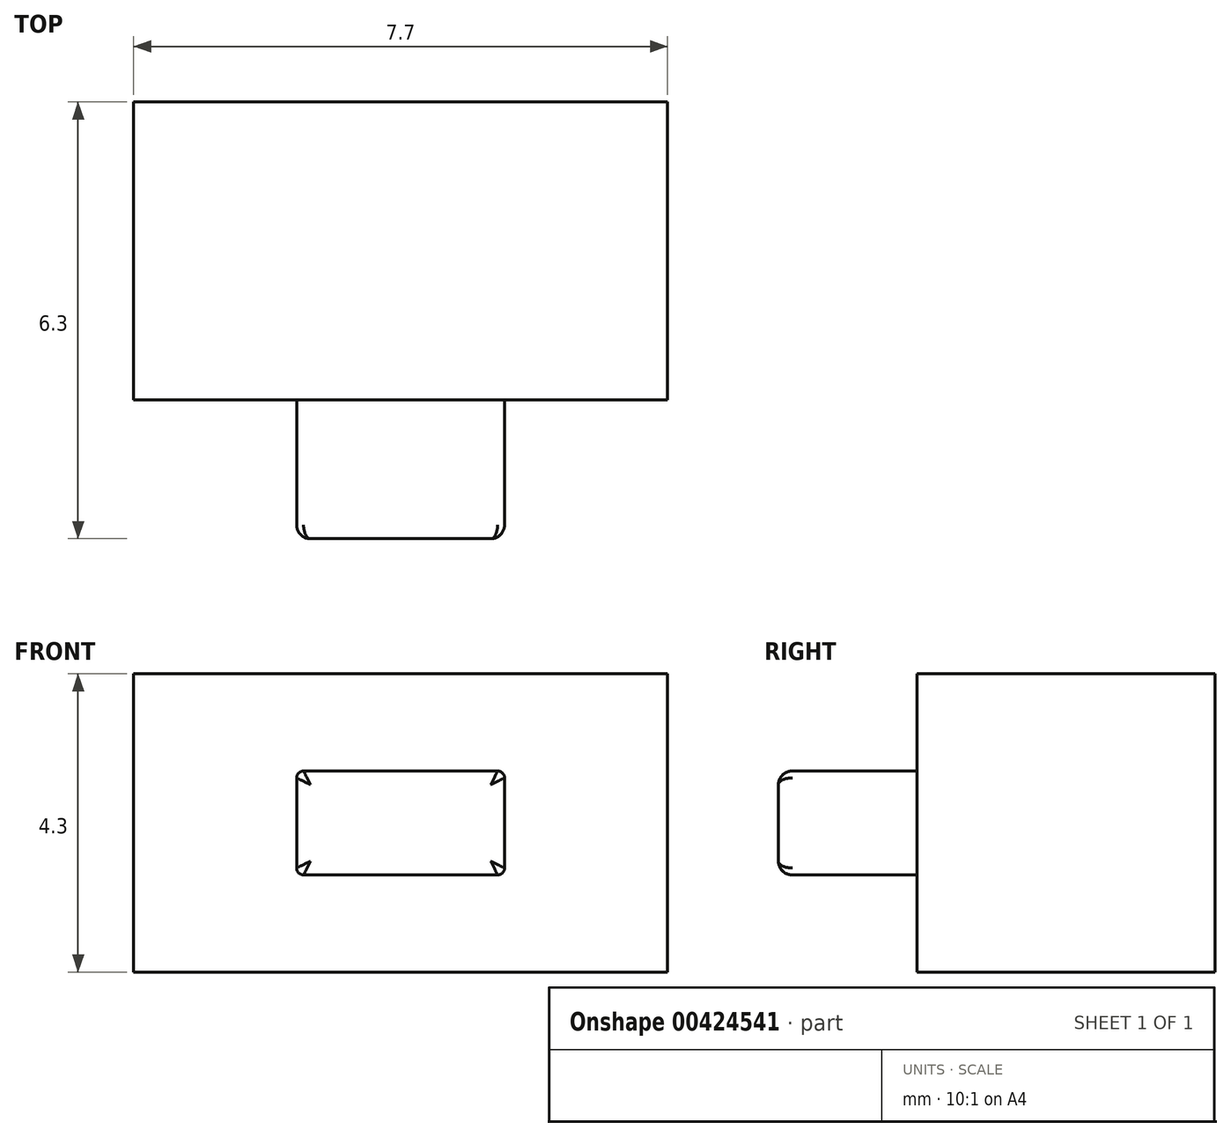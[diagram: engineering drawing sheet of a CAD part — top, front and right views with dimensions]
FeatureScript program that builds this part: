
annotation { "Feature Type Name" : "Feature", "Feature Type Description" : "" }
export const myFeature = defineFeature(function(context is Context, id is Id, definition is map)
    precondition{}
    {
        {
            var Q0;
            Q0=qCreatedBy(makeId("Front.planeOp"),FACE);
            var sketch = newSketch(context, id + "F0", { "sketchPlane" : qUnion([Q0])});
            skLineSegment(sketch, "E0.bottom", {"start": v(3.85, -2.15) * mm, "end": v(-3.85, -2.15) * mm});
            skLineSegment(sketch, "E0.top", {"start": v(3.85, 2.15) * mm, "end": v(-3.85, 2.15) * mm});
            skLineSegment(sketch, "E0.left", {"start": v(3.85, -2.15) * mm, "end": v(3.85, 2.15) * mm});
            skLineSegment(sketch, "E0.right", {"start": v(-3.85, -2.15) * mm, "end": v(-3.85, 2.15) * mm});
            skPoint(sketch, "E0.middle", {"position": v(0, 0) * mm});
            skLineSegment(sketch, "E1.bottom", {"start": v(1.5, -0.75) * mm, "end": v(-1.5, -0.75) * mm});
            skLineSegment(sketch, "E1.top", {"start": v(1.5, 0.75) * mm, "end": v(-1.5, 0.75) * mm});
            skLineSegment(sketch, "E1.left", {"start": v(1.5, -0.75) * mm, "end": v(1.5, 0.75) * mm});
            skLineSegment(sketch, "E1.right", {"start": v(-1.5, -0.75) * mm, "end": v(-1.5, 0.75) * mm});
            skSolve(sketch);
        }
        {
            var Q0;
            Q0=makeQuery(id+"F0.imprint","IMPRINT",FACE,{"disambiguationData":[TD([[makeQuery(id+"F0.imprint","IMPRINT",EDGE,{"derivedFrom":sQuery(id+"F0.wireOp",EDGE,"E0.bottom")}),-1.0]])]});
            var Q1;
            Q1=makeQuery(id+"F0.imprint","IMPRINT",FACE,{"disambiguationData":[TD([[makeQuery(id+"F0.imprint","IMPRINT",EDGE,{"derivedFrom":sQuery(id+"F0.wireOp",EDGE,"E1.bottom")}),-1.0]])]});
            extrude(context, id + "F1", {"entities" : qUnion([Q0, Q1]), "oppositeDirection" : true, "depth" : 4.3 * mm});
        }
        {
            var Q0;
            Q0=makeQuery(id+"F0.imprint","IMPRINT",FACE,{"disambiguationData":[TD([[makeQuery(id+"F0.imprint","IMPRINT",EDGE,{"derivedFrom":sQuery(id+"F0.wireOp",EDGE,"E1.bottom")}),-1.0]])]});
            extrude(context, id + "F2", {"entities" : qUnion([Q0]), "operationType" : NewBodyOperationType.ADD, "depth" : 2 * mm});
        }
        {
            var Q0;
            Q0=makeQuery(id+"F2.opExtrude","CAP_EDGE",EDGE,{"disambiguationData":[OSD([sQuery(id+"F0.wireOp",EDGE,"E1.top")])],"isStart":false});
            var Q1;
            Q1=makeQuery(id+"F2.opExtrude","CAP_EDGE",EDGE,{"disambiguationData":[OSD([sQuery(id+"F0.wireOp",EDGE,"E1.left")])],"isStart":false});
            var Q2;
            Q2=makeQuery(id+"F2.opExtrude","CAP_EDGE",EDGE,{"disambiguationData":[OSD([sQuery(id+"F0.wireOp",EDGE,"E1.bottom")])],"isStart":false});
            var Q3;
            Q3=makeQuery(id+"F2.opExtrude","CAP_EDGE",EDGE,{"disambiguationData":[OSD([sQuery(id+"F0.wireOp",EDGE,"E1.right")])],"isStart":false});
            fillet(context, id + "F3", {"entities" : qUnion([Q0, Q1, Q2, Q3]), "radius" : .2 * mm, "tangentPropagation" : true, "allowEdgeOverflow" : false});
        }
        {
            var Q0;
            Q0=makeQuery(id+"F3.opFillet","BLEND_EDGE",EDGE,{"blendedFrom":[makeQuery(id+"F2.opExtrude","CAP_EDGE",EDGE,{"disambiguationData":[OSD([sQuery(id+"F0.wireOp",EDGE,"E1.top")])],"isStart":false}),makeQuery(id+"F2.opExtrude","CAP_EDGE",EDGE,{"disambiguationData":[OSD([sQuery(id+"F0.wireOp",EDGE,"E1.left")])],"isStart":false})],"blendedInto":[]});
            var Q1;
            Q1=makeQuery(id+"F3.opFillet","BLEND_EDGE",EDGE,{"blendedFrom":[makeQuery(id+"F2.opExtrude","CAP_EDGE",EDGE,{"disambiguationData":[OSD([sQuery(id+"F0.wireOp",EDGE,"E1.bottom")])],"isStart":false}),makeQuery(id+"F2.opExtrude","CAP_EDGE",EDGE,{"disambiguationData":[OSD([sQuery(id+"F0.wireOp",EDGE,"E1.left")])],"isStart":false})],"blendedInto":[]});
            var Q2;
            Q2=makeQuery(id+"F3.opFillet","BLEND_EDGE",EDGE,{"blendedFrom":[makeQuery(id+"F2.opExtrude","CAP_EDGE",EDGE,{"disambiguationData":[OSD([sQuery(id+"F0.wireOp",EDGE,"E1.bottom")])],"isStart":false}),makeQuery(id+"F2.opExtrude","CAP_EDGE",EDGE,{"disambiguationData":[OSD([sQuery(id+"F0.wireOp",EDGE,"E1.right")])],"isStart":false})],"blendedInto":[]});
            var Q3;
            Q3=makeQuery(id+"F3.opFillet","BLEND_EDGE",EDGE,{"blendedFrom":[makeQuery(id+"F2.opExtrude","CAP_EDGE",EDGE,{"disambiguationData":[OSD([sQuery(id+"F0.wireOp",EDGE,"E1.top")])],"isStart":false}),makeQuery(id+"F2.opExtrude","CAP_EDGE",EDGE,{"disambiguationData":[OSD([sQuery(id+"F0.wireOp",EDGE,"E1.right")])],"isStart":false})],"blendedInto":[]});
            fillet(context, id + "F4", {"entities" : qUnion([Q0, Q1, Q2, Q3]), "radius" : .1 * mm, "tangentPropagation" : true, "allowEdgeOverflow" : false});
        }
    });
